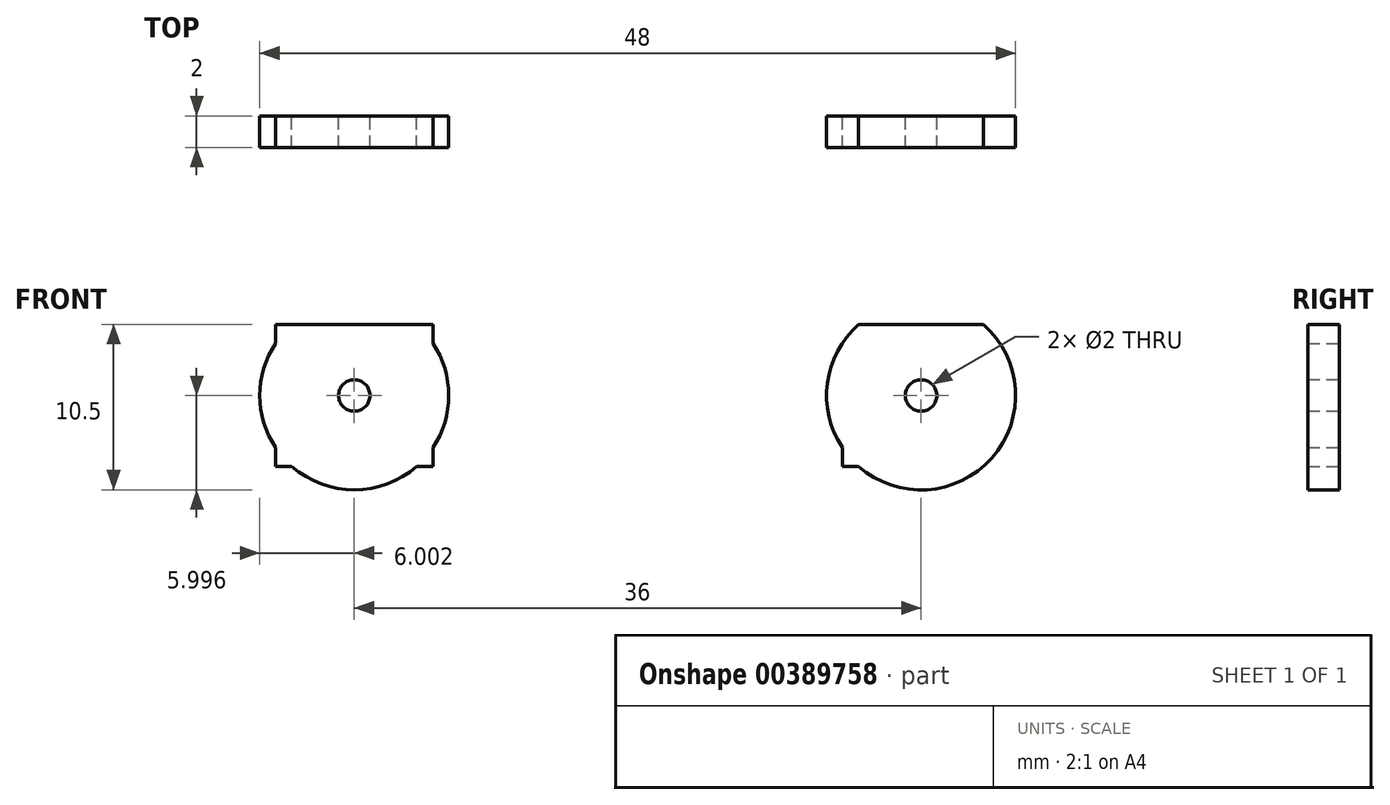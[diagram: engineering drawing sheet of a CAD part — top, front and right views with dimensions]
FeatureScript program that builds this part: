
annotation { "Feature Type Name" : "Feature", "Feature Type Description" : "" }
export const myFeature = defineFeature(function(context is Context, id is Id, definition is map)
    precondition{}
    {
        {
            var Q0;
            Q0=qCreatedBy(makeId("Front.planeOp"),FACE);
            var sketch = newSketch(context, id + "F0", { "sketchPlane" : qUnion([Q0])});
            skLineSegment(sketch, "E0.bottom", {"start": v(-58.9, 34.75) * mm, "end": v(-12.9, 34.75) * mm});
            skLineSegment(sketch, "E0.top", {"start": v(-58.9, 25.75) * mm, "end": v(-12.9, 25.75) * mm});
            skLineSegment(sketch, "E0.left", {"start": v(-58.9, 34.75) * mm, "end": v(-58.9, 25.75) * mm});
            skLineSegment(sketch, "E0.right", {"start": v(-12.9, 34.75) * mm, "end": v(-12.9, 25.75) * mm});
            skLineSegment(sketch, "E1", {"start": v(-48.9, 34.75) * mm, "end": v(-22.9, 34.75) * mm});
            skLineSegment(sketch, "E2", {"start": v(-58.9, 34.75) * mm, "end": v(-48.9, 34.75) * mm});
            skLineSegment(sketch, "E3", {"start": v(-22.9, 34.75) * mm, "end": v(-12.9, 34.75) * mm});
            skLineSegment(sketch, "E4", {"start": v(-22.9, 34.75) * mm, "end": v(-22.9, 25.75) * mm});
            skLineSegment(sketch, "E5", {"start": v(-22.9, 30.25) * mm, "end": v(-17.9, 30.25) * mm});
            skCircle(sketch, "E6", {"center": v(-17.9, 30.25) * mm, "radius": 6 * mm});
            skLineSegment(sketch, "E7", {"start": v(-48.9, 34.75) * mm, "end": v(-48.9, 25.75) * mm});
            skLineSegment(sketch, "E8", {"start": v(-48.9, 30.25) * mm, "end": v(-53.9, 30.25) * mm});
            skCircle(sketch, "E9", {"center": v(-53.9, 30.25) * mm, "radius": 6 * mm});
            skLineSegment(sketch, "E10", {"start": v(-58.9, 34.75) * mm, "end": v(-57.88, 34.75) * mm});
            skLineSegment(sketch, "E11", {"start": v(-58.9, 25.75) * mm, "end": v(-57.88, 25.75) * mm});
            skCircle(sketch, "E12", {"center": v(-17.9, 30.25) * mm, "radius": 1 * mm});
            skCircle(sketch, "E13", {"center": v(-53.9, 30.25) * mm, "radius": 1 * mm});
            skSolve(sketch);
        }
        {
            var Q0;
            {var subQ0=sQuery(id+"F0.wireOp",EDGE,"E0.left");var subQ1=sQuery(id+"F0.wireOp",EDGE,"E9");var subQ2=makeQuery(id+"F0.imprint","INTERSECT",VERTEX,{"disambiguationData":[OD(0.0)],"derivedFrom":[subQ1,subQ0]});Q0=makeQuery(id+"F0.imprint","IMPRINT",FACE,{"disambiguationData":[TD([[makeQuery(id+"F0.imprint","IMPRINT",EDGE,{"disambiguationData":[TD([[subQ2,-1.0]])],"derivedFrom":subQ1}),1.0]])]});}
            var Q1;
            {var subQ0=sQuery(id+"F0.wireOp",EDGE,"E9");var subQ1=sQuery(id+"F0.wireOp",EDGE,"E2");var subQ3=makeQuery(id+"F0.imprint","INTERSECT",VERTEX,{"derivedFrom":[subQ1,subQ0]});Q1=makeQuery(id+"F0.imprint","IMPRINT",FACE,{"disambiguationData":[TD([[makeQuery(id+"F0.imprint","IMPRINT",EDGE,{"disambiguationData":[TD([[subQ3,1.0]])],"derivedFrom":subQ1}),1.0]])]});}
            var Q2;
            {var subQ5=sQuery(id+"F0.wireOp",EDGE,"E1");Q2=makeQuery(id+"F0.imprint","IMPRINT",FACE,{"disambiguationData":[TD([[makeQuery(id+"F0.imprint","IMPRINT",EDGE,{"derivedFrom":subQ5}),-1.0]])]});}
            var Q3;
            {var subQ0=sQuery(id+"F0.wireOp",EDGE,"E7");var subQ1=makeQuery(id+"F0.imprint","IMPRINT",VERTEX,{"derivedFrom":subQ0});Q3=makeQuery(id+"F0.imprint","IMPRINT",FACE,{"disambiguationData":[TD([[makeQuery(id+"F0.imprint","IMPRINT",EDGE,{"disambiguationData":[TD([[subQ1,1.0]])],"derivedFrom":subQ0}),1.0]])]});}
            var Q4;
            {var subQ0=sQuery(id+"F0.wireOp",EDGE,"E9");var subQ1=sQuery(id+"F0.wireOp",EDGE,"E0.top");var subQ3=makeQuery(id+"F0.imprint","INTERSECT",VERTEX,{"derivedFrom":[subQ1,subQ0]});Q4=makeQuery(id+"F0.imprint","IMPRINT",FACE,{"disambiguationData":[TD([[makeQuery(id+"F0.imprint","IMPRINT",EDGE,{"disambiguationData":[TD([[subQ3,1.0]])],"derivedFrom":subQ1}),-1.0]])]});}
            var Q5;
            {var subQ0=sQuery(id+"F0.wireOp",EDGE,"E7");var subQ1=makeQuery(id+"F0.imprint","IMPRINT",VERTEX,{"derivedFrom":subQ0});Q5=makeQuery(id+"F0.imprint","IMPRINT",FACE,{"disambiguationData":[TD([[makeQuery(id+"F0.imprint","IMPRINT",EDGE,{"disambiguationData":[TD([[subQ1,1.0]])],"derivedFrom":subQ0}),-1.0]])]});}
            var Q6;
            {var subQ0=sQuery(id+"F0.wireOp",EDGE,"E4");var subQ1=makeQuery(id+"F0.imprint","IMPRINT",VERTEX,{"derivedFrom":subQ0});Q6=makeQuery(id+"F0.imprint","IMPRINT",FACE,{"disambiguationData":[TD([[makeQuery(id+"F0.imprint","IMPRINT",EDGE,{"disambiguationData":[TD([[subQ1,1.0]])],"derivedFrom":subQ0}),-1.0]])]});}
            var Q7;
            {var subQ0=sQuery(id+"F0.wireOp",EDGE,"E6");var subQ1=sQuery(id+"F0.wireOp",EDGE,"E3");var subQ2=makeQuery(id+"F0.imprint","INTERSECT",VERTEX,{"disambiguationData":[OD(0.0)],"derivedFrom":[subQ1,subQ0]});Q7=makeQuery(id+"F0.imprint","IMPRINT",FACE,{"disambiguationData":[TD([[makeQuery(id+"F0.imprint","IMPRINT",EDGE,{"disambiguationData":[TD([[subQ2,-1.0]])],"derivedFrom":subQ1}),1.0]])]});}
            var Q8;
            {var subQ0=sQuery(id+"F0.wireOp",EDGE,"E6");var subQ1=sQuery(id+"F0.wireOp",EDGE,"E0.right");var subQ2=makeQuery(id+"F0.imprint","INTERSECT",VERTEX,{"disambiguationData":[OD(0.0)],"derivedFrom":[subQ1,subQ0]});Q8=makeQuery(id+"F0.imprint","IMPRINT",FACE,{"disambiguationData":[TD([[makeQuery(id+"F0.imprint","IMPRINT",EDGE,{"disambiguationData":[TD([[subQ2,-1.0]])],"derivedFrom":subQ1}),1.0]])]});}
            var Q9;
            {var subQ0=sQuery(id+"F0.wireOp",EDGE,"E6");var subQ1=sQuery(id+"F0.wireOp",EDGE,"E0.top");var subQ2=makeQuery(id+"F0.imprint","INTERSECT",VERTEX,{"disambiguationData":[OD(0.0)],"derivedFrom":[subQ1,subQ0]});Q9=makeQuery(id+"F0.imprint","IMPRINT",FACE,{"disambiguationData":[TD([[makeQuery(id+"F0.imprint","IMPRINT",EDGE,{"disambiguationData":[TD([[subQ2,-1.0]])],"derivedFrom":subQ1}),-1.0]])]});}
            var Q10;
            {var subQ0=sQuery(id+"F0.wireOp",EDGE,"E7");var subQ1=sQuery(id+"F0.wireOp",EDGE,"E0.top");var subQ2=makeQuery(id+"F0.imprint","INTERSECT",VERTEX,{"derivedFrom":[subQ1,subQ0]});Q10=makeQuery(id+"F0.imprint","IMPRINT",FACE,{"disambiguationData":[TD([[makeQuery(id+"F0.imprint","IMPRINT",EDGE,{"disambiguationData":[TD([[subQ2,1.0]])],"derivedFrom":subQ1}),1.0]])]});}
            var Q11;
            {var subQ1=sQuery(id+"F0.wireOp",EDGE,"E2");var subQ3=sQuery(id+"F0.wireOp",EDGE,"E9");var subQ4=makeQuery(id+"F0.imprint","INTERSECT",VERTEX,{"derivedFrom":[subQ1,subQ3]});Q11=makeQuery(id+"F0.imprint","IMPRINT",FACE,{"disambiguationData":[TD([[makeQuery(id+"F0.imprint","IMPRINT",EDGE,{"disambiguationData":[TD([[subQ4,1.0]])],"derivedFrom":subQ3}),-1.0]])]});}
            var Q12;
            {var subQ1=sQuery(id+"F0.wireOp",EDGE,"E3");var subQ3=sQuery(id+"F0.wireOp",EDGE,"E6");var subQ4=makeQuery(id+"F0.imprint","INTERSECT",VERTEX,{"disambiguationData":[OD(0.0)],"derivedFrom":[subQ1,subQ3]});Q12=makeQuery(id+"F0.imprint","IMPRINT",FACE,{"disambiguationData":[TD([[makeQuery(id+"F0.imprint","IMPRINT",EDGE,{"disambiguationData":[TD([[subQ4,-1.0]])],"derivedFrom":subQ3}),-1.0]])]});}
            var Q13;
            {var subQ0=sQuery(id+"F0.wireOp",EDGE,"E4");var subQ1=makeQuery(id+"F0.imprint","IMPRINT",VERTEX,{"derivedFrom":subQ0});Q13=makeQuery(id+"F0.imprint","IMPRINT",FACE,{"disambiguationData":[TD([[makeQuery(id+"F0.imprint","IMPRINT",EDGE,{"disambiguationData":[TD([[subQ1,1.0]])],"derivedFrom":subQ0}),1.0]])]});}
            var Q14;
            {var subQ0=sQuery(id+"F0.wireOp",EDGE,"E4");var subQ1=sQuery(id+"F0.wireOp",EDGE,"E0.top");var subQ2=makeQuery(id+"F0.imprint","INTERSECT",VERTEX,{"derivedFrom":[subQ1,subQ0]});Q14=makeQuery(id+"F0.imprint","IMPRINT",FACE,{"disambiguationData":[TD([[makeQuery(id+"F0.imprint","IMPRINT",EDGE,{"disambiguationData":[TD([[subQ2,-1.0]])],"derivedFrom":subQ1}),1.0]])]});}
            extrude(context, id + "F1", {"entities" : qUnion([Q0, Q1, Q2, Q3, Q4, Q5, Q6, Q7, Q8, Q9, Q10, Q11, Q12, Q13, Q14]), "depth" : 2 * mm});
        }
    });
